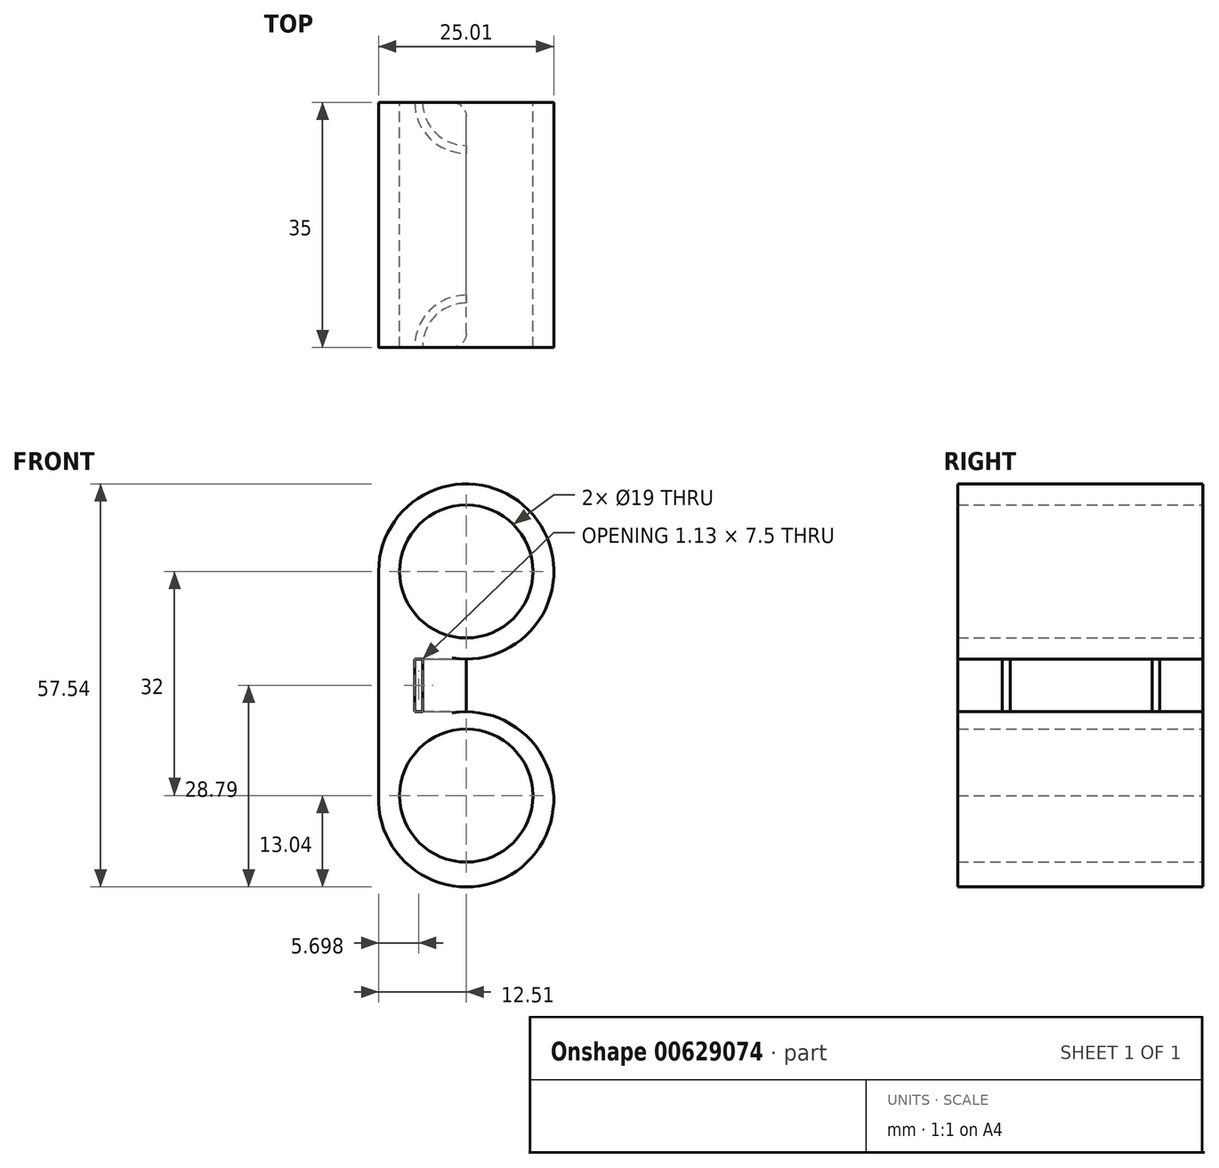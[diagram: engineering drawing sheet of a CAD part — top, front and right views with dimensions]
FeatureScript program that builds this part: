
annotation { "Feature Type Name" : "Feature", "Feature Type Description" : "" }
export const myFeature = defineFeature(function(context is Context, id is Id, definition is map)
    precondition{}
    {
        {
            var Q0;
            Q0=qCreatedBy(makeId("Front.planeOp"),FACE);
            var sketch = newSketch(context, id + "F0", { "sketchPlane" : qUnion([Q0])});
            skLineSegment(sketch, "E0", {"start": v(0, 0) * mm, "end": v(0, 32) * mm});
            skArc(sketch, "E1", {"start": v(12.5, 19.5) * mm, "mid": v(21.34, 40.84) * mm, "end": v(0, 32) * mm});
            skLineSegment(sketch, "E2", {"start": v(12.5, 19.5) * mm, "end": v(12.5, 11.96) * mm});
            skCircle(sketch, "E3", {"center": v(12.5, 32) * mm, "radius": 9.5 * mm});
            skCircle(sketch, "E4", {"center": v(12.5, 0) * mm, "radius": 9.5 * mm});
            skArc(sketch, "E5", {"start": v(0, 0) * mm, "mid": v(21.13, -9.58) * mm, "end": v(12.5, 11.96) * mm});
            skSolve(sketch);
        }
        {
            var Q0;
            Q0 = qSketchRegion(id + "F0", true);
            extrude(context, id + "F1", {"entities" : qUnion([Q0]), "depth" : 35 * mm, "offsetDistance" : 25 * mm});
        }
        {
            var Q0;
            Q0=qCreatedBy(makeId("Top.planeOp"),FACE);
            cPlane(context, id + "F2", {"entities" : qUnion([Q0]), "cplaneType" : CPlaneType.OFFSET, "offset" : 12 * mm, "width" : 150 * mm, "height" : 150 * mm});
        }
        {
            var Q0;
            Q0=qCreatedBy(id+"F2.planeOp",FACE);
            var sketch = newSketch(context, id + "F3", { "sketchPlane" : qUnion([Q0])});
            skArc(sketch, "E6", {"start": v(6.25, 0) * mm, "mid": v(8.11, -4.37) * mm, "end": v(12.5, -6.17) * mm});
            skArc(sketch, "E7", {"start": v(5.13, 0) * mm, "mid": v(7.31, -5.16) * mm, "end": v(12.5, -7.3) * mm});
            skLineSegment(sketch, "E8", {"start": v(12.5, -6.17) * mm, "end": v(12.5, -7.3) * mm});
            skLineSegment(sketch, "E9", {"start": v(12.5, -27.54) * mm, "end": v(12.5, -28.67) * mm});
            skArc(sketch, "E10", {"start": v(12.5, -27.54) * mm, "mid": v(7.26, -29.73) * mm, "end": v(5.13, -35) * mm});
            skArc(sketch, "E11", {"start": v(12.5, -28.67) * mm, "mid": v(8.05, -30.53) * mm, "end": v(6.25, -35) * mm});
            skLineSegment(sketch, "E12", {"start": v(6.25, 0) * mm, "end": v(5.13, 0) * mm});
            skLineSegment(sketch, "E13", {"start": v(5.13, -35) * mm, "end": v(6.25, -35) * mm});
            skSolve(sketch);
        }
        {
            var Q0;
            Q0 = qSketchRegion(id + "F3", true);
            extrude(context, id + "F4", {"entities" : qUnion([Q0]), "operationType" : NewBodyOperationType.REMOVE, "depth" : 7.5 * mm, "offsetDistance" : 25 * mm});
        }
        {
            var Q0;
            Q0=makeQuery(id+"F4.boolean.opBoolean","COPY",EDGE,{"derivedFrom":makeQuery(id+"F4.opExtrude","SWEPT_EDGE",EDGE,{"disambiguationData":[OSD([sQuery(id+"F3.wireOp",EDGE,"E9"),sQuery(id+"F3.wireOp",EDGE,"E11")])]})});
            var Q1;
            Q1=makeQuery(id+"F1.opExtrude","CAP_EDGE",EDGE,{"disambiguationData":[OSD([sQuery(id+"F0.wireOp",EDGE,"E2")])],"isStart":false});
            var Q2;
            Q2=makeQuery(id+"F4.boolean.opBoolean","COPY",EDGE,{"derivedFrom":makeQuery(id+"F4.opExtrude","SWEPT_EDGE",EDGE,{"disambiguationData":[OSD([sQuery(id+"F3.wireOp",EDGE,"E6"),sQuery(id+"F3.wireOp",EDGE,"E8")])]})});
            var Q3;
            Q3=makeQuery(id+"F1.opExtrude","CAP_EDGE",EDGE,{"disambiguationData":[OSD([sQuery(id+"F0.wireOp",EDGE,"E2")])],"isStart":true});
            fillet(context, id + "F5", {"entities" : qUnion([Q0, Q1, Q2, Q3]), "radius" : 2 * mm, "tangentPropagation" : true, "allowEdgeOverflow" : false});
        }
    });
